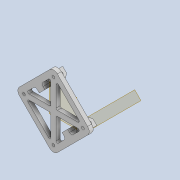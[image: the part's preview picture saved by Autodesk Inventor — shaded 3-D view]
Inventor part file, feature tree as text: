
AUTODESK INVENTOR PART (.ipt)
format: ipt  version: 2020 (Build 240168000, 168)  size: 286,208 bytes
history: native  units: mm
features: extrude x5, sketch x5, other x5, fillet x4, reference x4, projected_geometry x4, plane x2, chamfer x1
ambient origin geometry x8: Origin, YZ Plane, XZ Plane, XY Plane, X Axis, Y Axis, Z Axis, Center Point
bodies: Solid1 (feature_tree)
feature tree (30):
  plane  "Work Plane1"
  extrude  "Extrusion1"  Depth=40.0mm
  plane  "Work Plane2"
  extrude  "Extrusion2"  Depth=4.0mm
  extrude  "Extrusion3"  Depth=3.0mm
  extrude  "Extrusion4"  Depth=4.0mm
  fillet  "Fillet1"  Radius=6.0mm
  fillet  "Fillet2"  Radius=6.0mm
  chamfer  "Chamfer1"  Distance=6.0mm
  fillet  "Fillet3"  Radius=4.0mm
  extrude  "Extrusion5"  Depth=4.0mm TaperAngle=0.0deg
  fillet  "Fillet4"  Radius=8.0mm
  sketch  "Sketch1"  dims[d0=40.0mm d1=40.0mm]
  reference  "Reference1"
  reference  "Reference2"
  sketch  "Sketch2"  dims[d2=4.0mm d3=4.0mm]
  reference  "Reference3"
  reference  "Reference4"
  sketch  "Sketch3"  dims[d4=3.0mm d5=0.0mm d6=6.0mm]
  projected_geometry  "Projected Loop1"
  projected_geometry  "Projected Loop2"
  sketch  "Sketch4"  dims[d7=6.0mm d8=6.0mm d9=6.0mm d10=6.0mm d11=0.0mm d12=6.0mm d13=0.0mm d14=4.0mm]
  projected_geometry  "Projected Loop3"
  sketch  "Sketch5"  dims[d15=4.0mm d16=6.0mm d17=0.0mm d18=8.0mm d19=2.0mm d20=2.0mm d21=2.0mm d22=45.0deg d23=1.0mm d24=22.0mm d25=2.0mm d26=22.0mm d27=22.0mm d28=22.0mm d29=2.0mm d30=2.0mm d31=2.0mm d32=6.0mm d33=0.0mm d34=4.0mm]
  projected_geometry  "Projected Loop4"
  parser-record x1  (decoder bookkeeping rows leaked as tree rows — omitted from the tree; the rows remain in map.json)
  other  "tip_3_ass_base.iam"
  other  "mot_27_ass:1"
  other  "mot_27_2:1"
  other  "mot_test_enc_hh_1:1"
note: 1 file-system path scrubbed to <path> (originals preserved in map.json)
